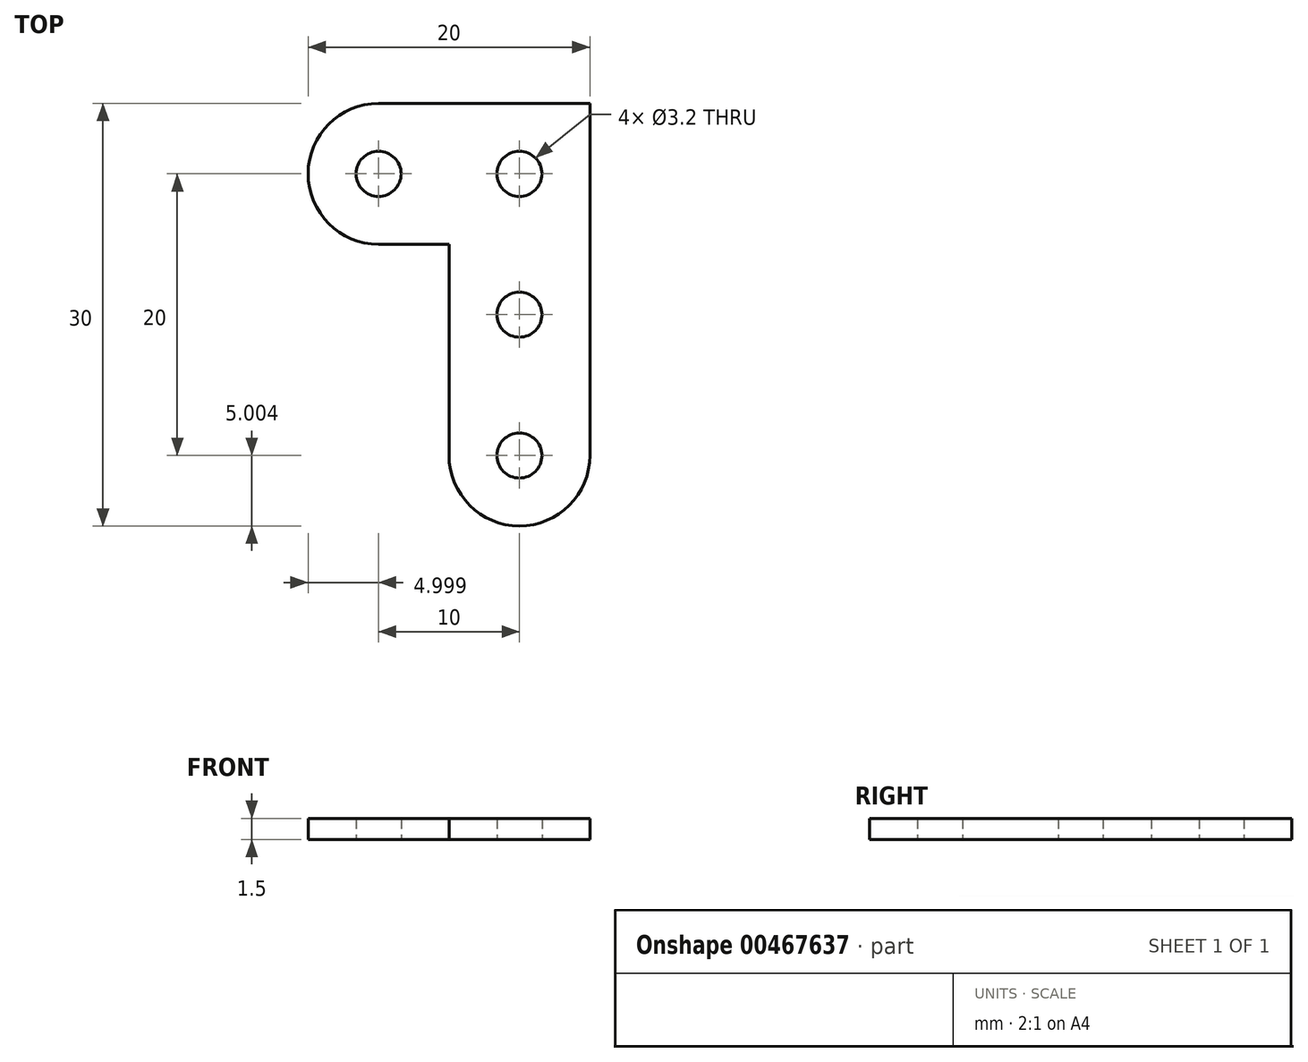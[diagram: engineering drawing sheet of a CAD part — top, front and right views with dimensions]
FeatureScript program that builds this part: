
annotation { "Feature Type Name" : "Feature", "Feature Type Description" : "" }
export const myFeature = defineFeature(function(context is Context, id is Id, definition is map)
    precondition{}
    {
        {
            var Q0;
            Q0=qCreatedBy(makeId("Top.planeOp"),FACE);
            var sketch = newSketch(context, id + "F0", { "sketchPlane" : qUnion([Q0])});
            skLineSegment(sketch, "E0.bottom", {"start": v(-58.07, 22.9) * mm, "end": v(-43.07, 22.9) * mm});
            skLineSegment(sketch, "E0.top", {"start": v(-58.07, 12.9) * mm, "end": v(-43.07, 12.9) * mm});
            skLineSegment(sketch, "E0.left", {"start": v(-63.07, 17.9) * mm, "end": v(-63.07, 17.9) * mm});
            skLineSegment(sketch, "E0.right", {"start": v(-43.07, 22.9) * mm, "end": v(-43.07, 12.9) * mm});
            skLineSegment(sketch, "E1", {"start": v(-43.07, 12.9) * mm, "end": v(-43.07, -2.1) * mm});
            skLineSegment(sketch, "E2", {"start": v(-48.07, -7.1) * mm, "end": v(-48.07, -7.1) * mm});
            skLineSegment(sketch, "E3", {"start": v(-53.07, -2.1) * mm, "end": v(-53.07, 12.9) * mm});
            skPoint(sketch, "E3.endSnap0", {"position": v(-53.07, 12.9) * mm});
            skCircle(sketch, "E4", {"center": v(-58.07, 17.9) * mm, "radius": 1.6 * mm});
            skCircle(sketch, "E5", {"center": v(-48.07, 17.9) * mm, "radius": 1.6 * mm});
            skCircle(sketch, "E6", {"center": v(-48.07, 7.9) * mm, "radius": 1.6 * mm});
            skCircle(sketch, "E7", {"center": v(-48.07, -2.1) * mm, "radius": 1.6 * mm});
            skPoint(sketch, "E8.visualSharp", {"position": v(-63.07, 22.9) * mm});
            skArc(sketch, "E8.filletArc", {"start": v(-58.07, 22.9) * mm, "mid": v(-61.6, 21.43) * mm, "end": v(-63.07, 17.9) * mm});
            skPoint(sketch, "E9.visualSharp", {"position": v(-63.07, 12.9) * mm});
            skArc(sketch, "E9.filletArc", {"start": v(-63.07, 17.9) * mm, "mid": v(-61.6, 14.36) * mm, "end": v(-58.07, 12.9) * mm});
            skPoint(sketch, "E10.visualSharp", {"position": v(-53.07, -7.1) * mm});
            skArc(sketch, "E10.filletArc", {"start": v(-53.07, -2.1) * mm, "mid": v(-51.6, -5.64) * mm, "end": v(-48.07, -7.1) * mm});
            skPoint(sketch, "E11.visualSharp", {"position": v(-43.07, -7.1) * mm});
            skArc(sketch, "E11.filletArc", {"start": v(-48.07, -7.1) * mm, "mid": v(-44.54, -5.64) * mm, "end": v(-43.07, -2.1) * mm});
            skSolve(sketch);
        }
        {
            var Q0;
            Q0 = qSketchRegion(id + "F0", true);
            extrude(context, id + "F1", {"entities" : qUnion([Q0]), "depth" : 1.5 * mm});
        }
    });
